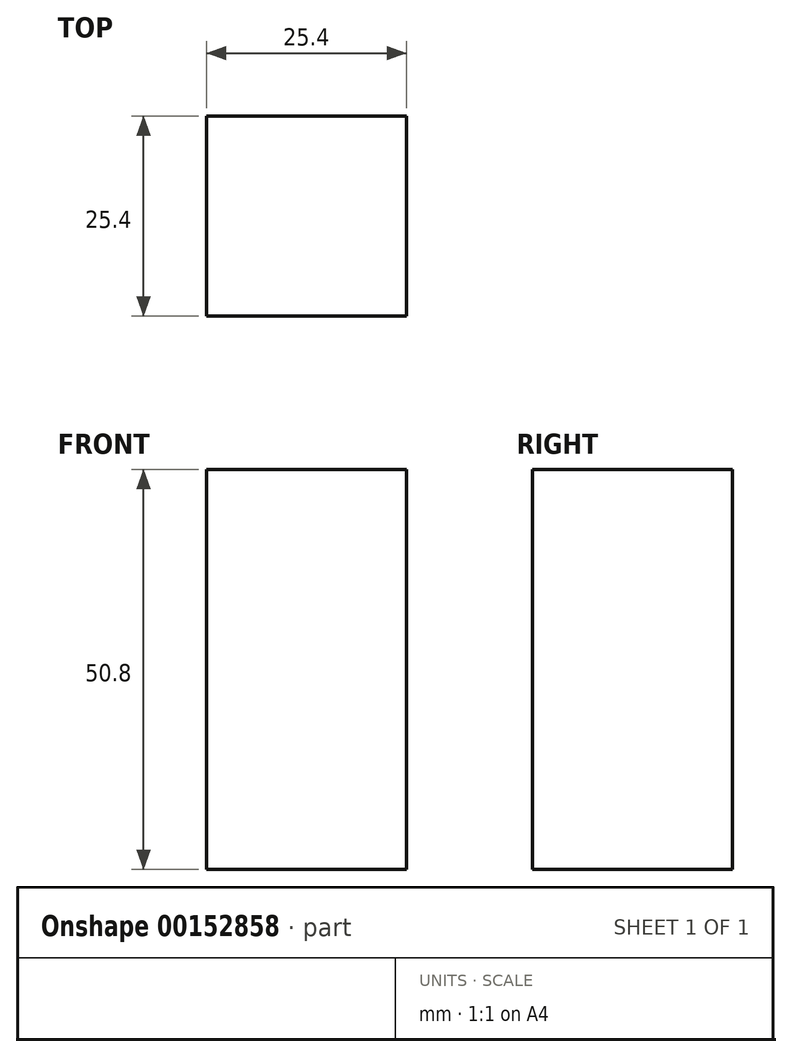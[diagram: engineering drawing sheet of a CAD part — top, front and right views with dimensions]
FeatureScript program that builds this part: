
annotation { "Feature Type Name" : "Feature", "Feature Type Description" : "" }
export const myFeature = defineFeature(function(context is Context, id is Id, definition is map)
    precondition{}
    {
        {
            var Q0;
            Q0=qCreatedBy(makeId("Top.planeOp"),FACE);
            var sketch = newSketch(context, id + "F0", { "sketchPlane" : qUnion([Q0])});
            skLineSegment(sketch, "E0.bottom", {"start": v(12.7, -12.7) * mm, "end": v(-12.7, -12.7) * mm});
            skLineSegment(sketch, "E0.top", {"start": v(12.7, 12.7) * mm, "end": v(-12.7, 12.7) * mm});
            skLineSegment(sketch, "E0.left", {"start": v(12.7, -12.7) * mm, "end": v(12.7, 12.7) * mm});
            skLineSegment(sketch, "E0.right", {"start": v(-12.7, -12.7) * mm, "end": v(-12.7, 12.7) * mm});
            skPoint(sketch, "E0.middle", {"position": v(0, 0) * mm});
            skSolve(sketch);
        }
        {
            var Q0;
            Q0=qSketchRegion(id+"F0",true);
            extrude(context, id + "F1", {"entities" : qUnion([Q0]), "depth" : 50.8 * mm});
        }
    });
